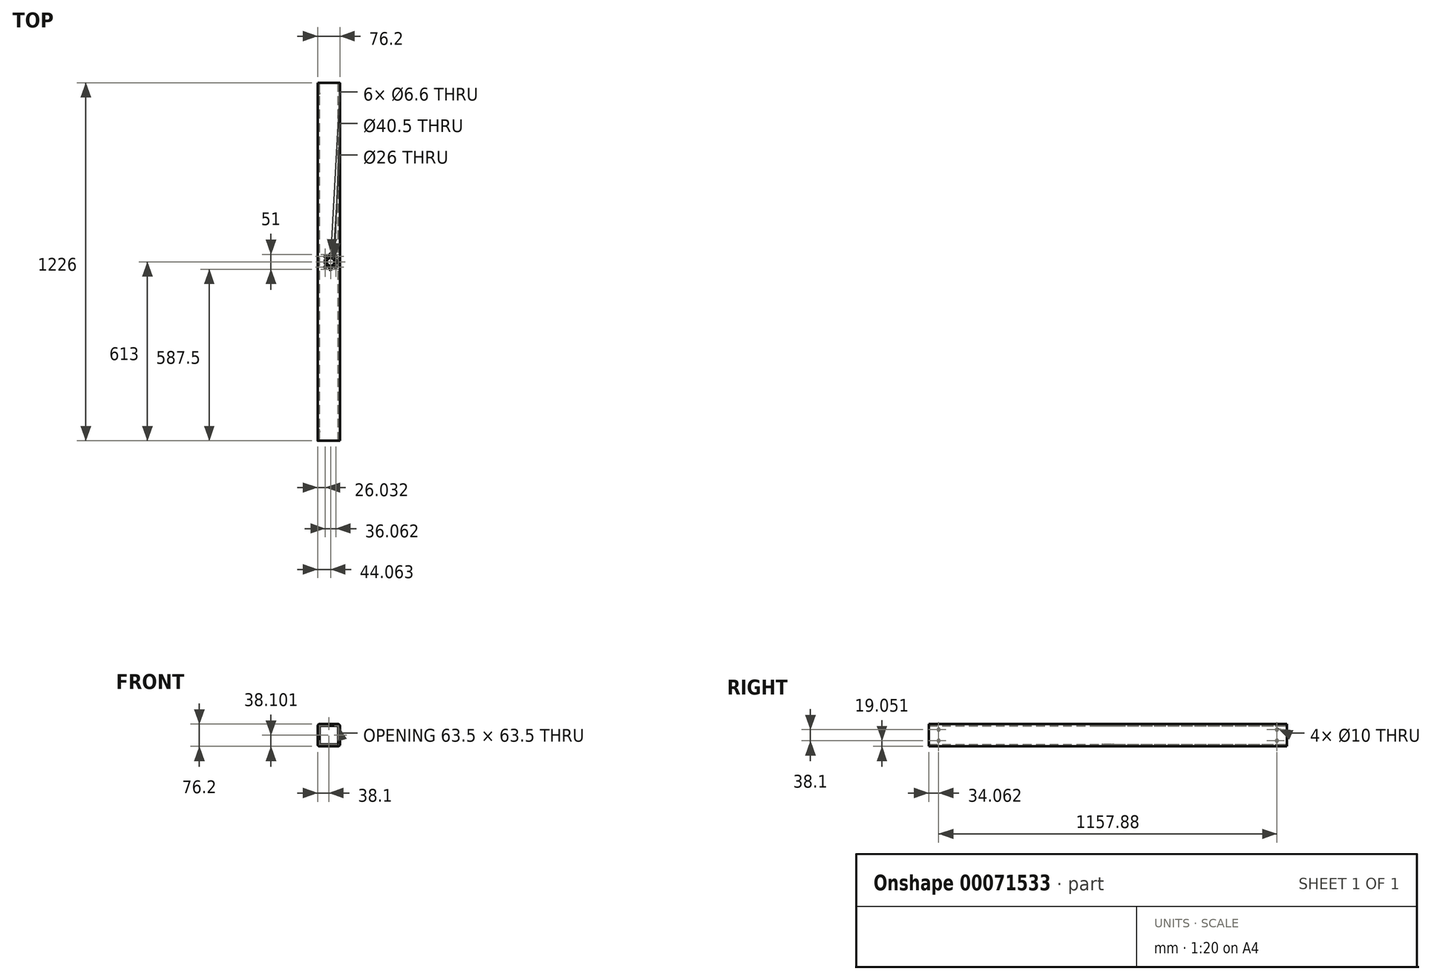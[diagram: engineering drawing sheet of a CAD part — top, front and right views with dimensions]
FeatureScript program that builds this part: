
annotation { "Feature Type Name" : "Feature", "Feature Type Description" : "" }
export const myFeature = defineFeature(function(context is Context, id is Id, definition is map)
    precondition{}
    {
        {
            var Q0;
            Q0=qCreatedBy(makeId("Front.planeOp"),FACE);
            var sketch = newSketch(context, id + "F0", { "sketchPlane" : qUnion([Q0])});
            skLineSegment(sketch, "E0.bottom", {"start": v(-12.7, 36.7) * mm, "end": v(50.8, 36.7) * mm});
            skLineSegment(sketch, "E0.top", {"start": v(-12.7, -39.5) * mm, "end": v(50.8, -39.5) * mm});
            skLineSegment(sketch, "E0.left", {"start": v(-19.05, 30.34) * mm, "end": v(-19.05, -33.16) * mm});
            skLineSegment(sketch, "E0.right", {"start": v(57.15, 30.34) * mm, "end": v(57.15, -33.16) * mm});
            skLineSegment(sketch, "E1.bottom", {"start": v(-6.35, 30.34) * mm, "end": v(44.45, 30.34) * mm});
            skLineSegment(sketch, "E1.top", {"start": v(-6.35, -33.16) * mm, "end": v(44.45, -33.16) * mm});
            skLineSegment(sketch, "E1.left", {"start": v(-12.7, 24) * mm, "end": v(-12.7, -26.8) * mm});
            skLineSegment(sketch, "E1.right", {"start": v(50.8, 24) * mm, "end": v(50.8, -26.8) * mm});
            skPoint(sketch, "E2.visualSharp", {"position": v(-12.7, 30.34) * mm});
            skArc(sketch, "E2.filletArc", {"start": v(-6.35, 30.34) * mm, "mid": v(-10.84, 28.48) * mm, "end": v(-12.7, 24) * mm});
            skPoint(sketch, "E3.visualSharp", {"position": v(50.8, 30.34) * mm});
            skArc(sketch, "E3.filletArc", {"start": v(50.8, 24) * mm, "mid": v(48.94, 28.48) * mm, "end": v(44.45, 30.34) * mm});
            skPoint(sketch, "E4.visualSharp", {"position": v(50.8, -33.16) * mm});
            skArc(sketch, "E4.filletArc", {"start": v(44.45, -33.16) * mm, "mid": v(48.94, -31.3) * mm, "end": v(50.8, -26.8) * mm});
            skPoint(sketch, "E5.visualSharp", {"position": v(-12.7, -33.16) * mm});
            skArc(sketch, "E5.filletArc", {"start": v(-12.7, -26.8) * mm, "mid": v(-10.84, -31.3) * mm, "end": v(-6.35, -33.16) * mm});
            skPoint(sketch, "E6.visualSharp", {"position": v(57.15, -39.5) * mm});
            skArc(sketch, "E6.filletArc", {"start": v(50.8, -39.5) * mm, "mid": v(55.3, -37.65) * mm, "end": v(57.15, -33.16) * mm});
            skPoint(sketch, "E7.visualSharp", {"position": v(-19.05, -39.5) * mm});
            skArc(sketch, "E7.filletArc", {"start": v(-19.05, -33.16) * mm, "mid": v(-17.2, -37.65) * mm, "end": v(-12.7, -39.5) * mm});
            skPoint(sketch, "E8.visualSharp", {"position": v(57.15, 36.7) * mm});
            skArc(sketch, "E8.filletArc", {"start": v(57.15, 30.34) * mm, "mid": v(55.3, 34.83) * mm, "end": v(50.8, 36.7) * mm});
            skPoint(sketch, "E9.visualSharp", {"position": v(-19.05, 36.7) * mm});
            skArc(sketch, "E9.filletArc", {"start": v(-12.7, 36.7) * mm, "mid": v(-17.2, 34.83) * mm, "end": v(-19.05, 30.34) * mm});
            skSolve(sketch);
        }
        {
            var Q0;
            Q0=qSketchRegion(id+"F0",true);
            extrude(context, id + "F1", {"entities" : qUnion([Q0]), "depth" : 1226 * mm});
        }
        {
            var Q0;
            Q0=makeQuery(id+"F1.opExtrude","SWEPT_FACE",FACE,{"disambiguationData":[OSD([sQuery(id+"F0.wireOp",EDGE,"E0.left")])]});
            var sketch = newSketch(context, id + "F2", { "sketchPlane" : qUnion([Q0])});
            skCircle(sketch, "E10", {"center": v(34.06, 17.64) * mm, "radius": 5 * mm});
            skCircle(sketch, "E11", {"center": v(34.06, -20.46) * mm, "radius": 5 * mm});
            skCircle(sketch, "E12", {"center": v(1191.94, -20.46) * mm, "radius": 5 * mm});
            skCircle(sketch, "E13", {"center": v(1191.94, 17.64) * mm, "radius": 5 * mm});
            skSolve(sketch);
        }
        {
            var Q0;
            Q0=qSketchRegion(id+"F2",true);
            extrude(context, id + "F3", {"entities" : qUnion([Q0]), "operationType" : NewBodyOperationType.REMOVE, "oppositeDirection" : true, "depth" : 25.4 * mm});
        }
        {
            var Q0;
            Q0=makeQuery(id+"F1.opExtrude","SWEPT_FACE",FACE,{"disambiguationData":[OSD([sQuery(id+"F0.wireOp",EDGE,"E0.top")])]});
            var sketch = newSketch(context, id + "F4", { "sketchPlane" : qUnion([Q0])});
            skCircle(sketch, "E14", {"center": v(25.01, 638.5) * mm, "radius": 3.3 * mm});
            skCircle(sketch, "E15.1.0", {"center": v(6.98, 631.03) * mm, "radius": 3.3 * mm});
            skCircle(sketch, "E15.3.0", {"center": v(6.98, 594.97) * mm, "radius": 3.3 * mm});
            skCircle(sketch, "E15.4.0", {"center": v(25.01, 587.5) * mm, "radius": 3.3 * mm});
            skCircle(sketch, "E15.5.0", {"center": v(43.04, 594.97) * mm, "radius": 3.3 * mm});
            skCircle(sketch, "E15.7.0", {"center": v(43.04, 631.03) * mm, "radius": 3.3 * mm});
            skPoint(sketch, "E15.center", {"position": v(25.01, 613) * mm});
            skCircle(sketch, "E16", {"center": v(25.01, 613) * mm, "radius": 20.25 * mm});
            skSolve(sketch);
        }
        {
            var Q0;
            Q0 = qSketchRegion(id + "F4", true);
            extrude(context, id + "F5", {"entities" : qUnion([Q0]), "operationType" : NewBodyOperationType.REMOVE, "endBound" : BoundingType.THROUGH_ALL, "oppositeDirection" : true, "depth" : 25 * mm});
        }
        {
            var Q0;
            Q0=makeQuery(id+"F1.opExtrude","SWEPT_FACE",FACE,{"disambiguationData":[OSD([sQuery(id+"F0.wireOp",EDGE,"E0.top")])]});
            var sketch = newSketch(context, id + "F6", { "sketchPlane" : qUnion([Q0])});
            skLineSegment(sketch, "E17.bottom", {"start": v(-3.84, 541.7) * mm, "end": v(48.13, 541.7) * mm});
            skLineSegment(sketch, "E17.top", {"start": v(-3.84, 699.59) * mm, "end": v(48.13, 699.59) * mm});
            skLineSegment(sketch, "E17.left", {"start": v(-3.84, 541.7) * mm, "end": v(-3.84, 699.59) * mm});
            skLineSegment(sketch, "E17.right", {"start": v(48.13, 541.7) * mm, "end": v(48.13, 699.59) * mm});
            skCircle(sketch, "E18", {"center": v(25.01, 613) * mm, "radius": 13 * mm});
            skSolve(sketch);
        }
        {
            var Q0;
            Q0 = qSketchRegion(id + "F6", true);
            extrude(context, id + "F7", {"entities" : qUnion([Q0]), "operationType" : NewBodyOperationType.ADD, "oppositeDirection" : true, "depth" : 6.35 * mm});
        }
    });
